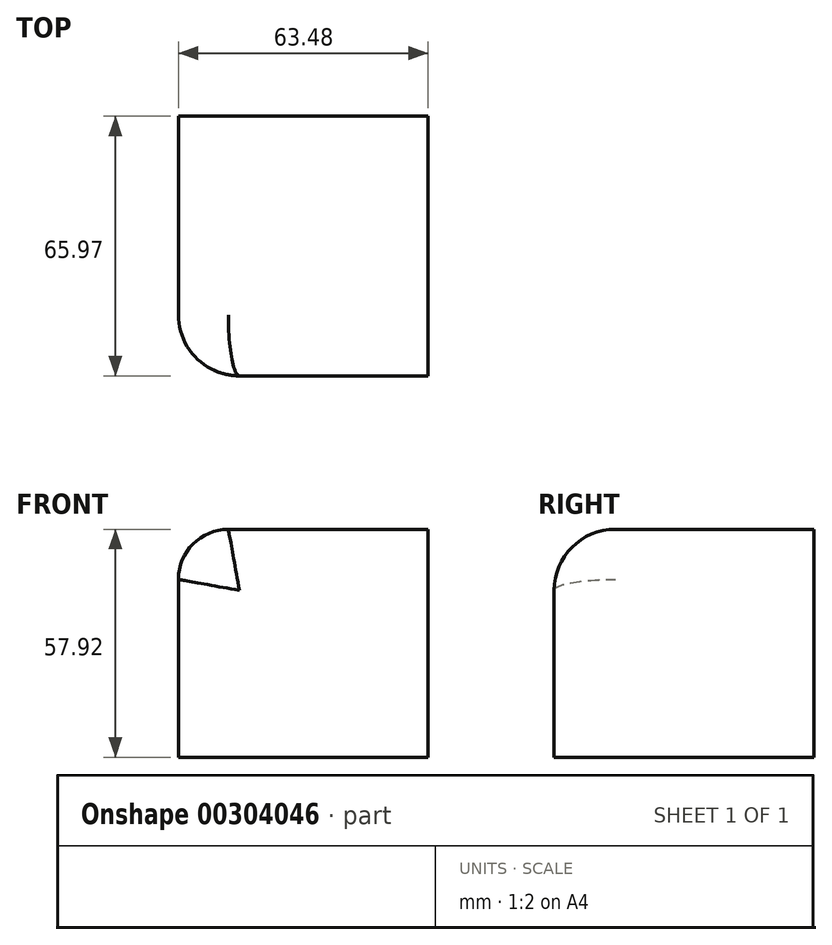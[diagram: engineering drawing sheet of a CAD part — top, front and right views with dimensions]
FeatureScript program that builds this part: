
annotation { "Feature Type Name" : "Feature", "Feature Type Description" : "" }
export const myFeature = defineFeature(function(context is Context, id is Id, definition is map)
    precondition{}
    {
        {
            var Q0;
            Q0=qCreatedBy(makeId("Top.planeOp"),FACE);
            var sketch = newSketch(context, id + "F0", { "sketchPlane" : qUnion([Q0])});
            skLineSegment(sketch, "E0.bottom", {"start": v(-32.78, -33.1) * mm, "end": v(30.7, -33.1) * mm});
            skLineSegment(sketch, "E0.top", {"start": v(-32.78, 32.87) * mm, "end": v(30.7, 32.87) * mm});
            skLineSegment(sketch, "E0.left", {"start": v(-32.78, -33.1) * mm, "end": v(-32.78, 32.87) * mm});
            skLineSegment(sketch, "E0.right", {"start": v(30.7, -33.1) * mm, "end": v(30.7, 32.87) * mm});
            skSolve(sketch);
        }
        {
            var Q0;
            Q0=makeQuery(id+"F0.imprint","IMPRINT",FACE,{"disambiguationData":[TD([[makeQuery(id+"F0.imprint","IMPRINT",EDGE,{"derivedFrom":sQuery(id+"F0.wireOp",EDGE,"E0.bottom")}),1.0]])]});
            extrude(context, id + "F1", {"entities" : qUnion([Q0]), "depth" : 57.92 * mm});
        }
        {
            var Q0;
            Q0=makeQuery(id+"F1.opExtrude","CAP_EDGE",EDGE,{"disambiguationData":[OSD([sQuery(id+"F0.wireOp",EDGE,"E0.left")])],"isStart":false});
            fillet(context, id + "F2", {"entities" : qUnion([Q0]), "radius" : 12.7 * mm, "tangentPropagation" : true, "allowEdgeOverflow" : false});
        }
        {
            var Q0;
            Q0=makeQuery(id+"F1.opExtrude","SWEPT_EDGE",EDGE,{"disambiguationData":[OSD([sQuery(id+"F0.wireOp",EDGE,"E0.bottom"),sQuery(id+"F0.wireOp",EDGE,"E0.left")])]});
            fillet(context, id + "F3", {"entities" : qUnion([Q0]), "radius" : 15.52 * mm, "tangentPropagation" : true, "allowEdgeOverflow" : false});
        }
    });
